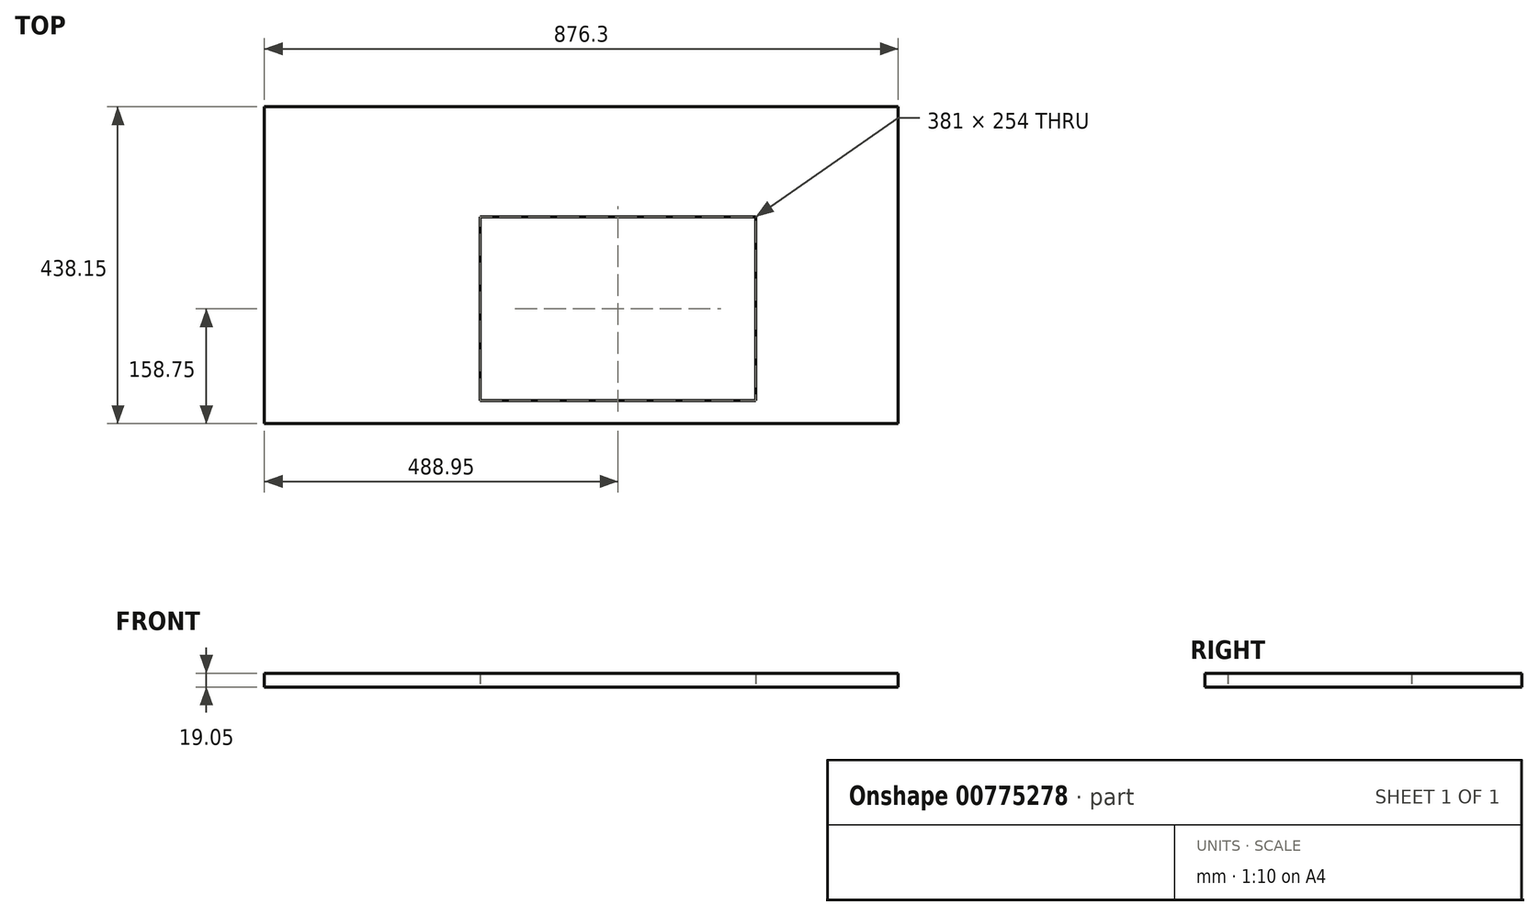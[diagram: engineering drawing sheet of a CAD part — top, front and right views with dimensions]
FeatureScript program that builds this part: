
annotation { "Feature Type Name" : "Feature", "Feature Type Description" : "" }
export const myFeature = defineFeature(function(context is Context, id is Id, definition is map)
    precondition{}
    {
        {
            var Q0;
            Q0=qCreatedBy(makeId("Top.planeOp"),FACE);
            var sketch = newSketch(context, id + "F0", { "sketchPlane" : qUnion([Q0])});
            skLineSegment(sketch, "E0.bottom", {"start": v(0, 0) * mm, "end": v(-876.3, 0) * mm});
            skLineSegment(sketch, "E0.top", {"start": v(0, 438.15) * mm, "end": v(-876.3, 438.15) * mm});
            skLineSegment(sketch, "E0.left", {"start": v(0, 0) * mm, "end": v(0, 438.15) * mm});
            skLineSegment(sketch, "E0.right", {"start": v(-876.3, 0) * mm, "end": v(-876.3, 438.15) * mm});
            skLineSegment(sketch, "E1.bottom", {"start": v(-577.85, 285.75) * mm, "end": v(-196.85, 285.75) * mm});
            skLineSegment(sketch, "E1.top", {"start": v(-577.85, 31.75) * mm, "end": v(-196.85, 31.75) * mm});
            skLineSegment(sketch, "E1.left", {"start": v(-577.85, 285.75) * mm, "end": v(-577.85, 31.75) * mm});
            skLineSegment(sketch, "E1.right", {"start": v(-196.85, 285.75) * mm, "end": v(-196.85, 31.75) * mm});
            skSolve(sketch);
        }
        {
            var Q0;
            Q0 = qSketchRegion(id + "F0", true);
            extrude(context, id + "F1", {"entities" : qUnion([Q0]), "depth" : 19.05 * mm, "offsetDistance" : 25.4 * mm});
        }
    });
